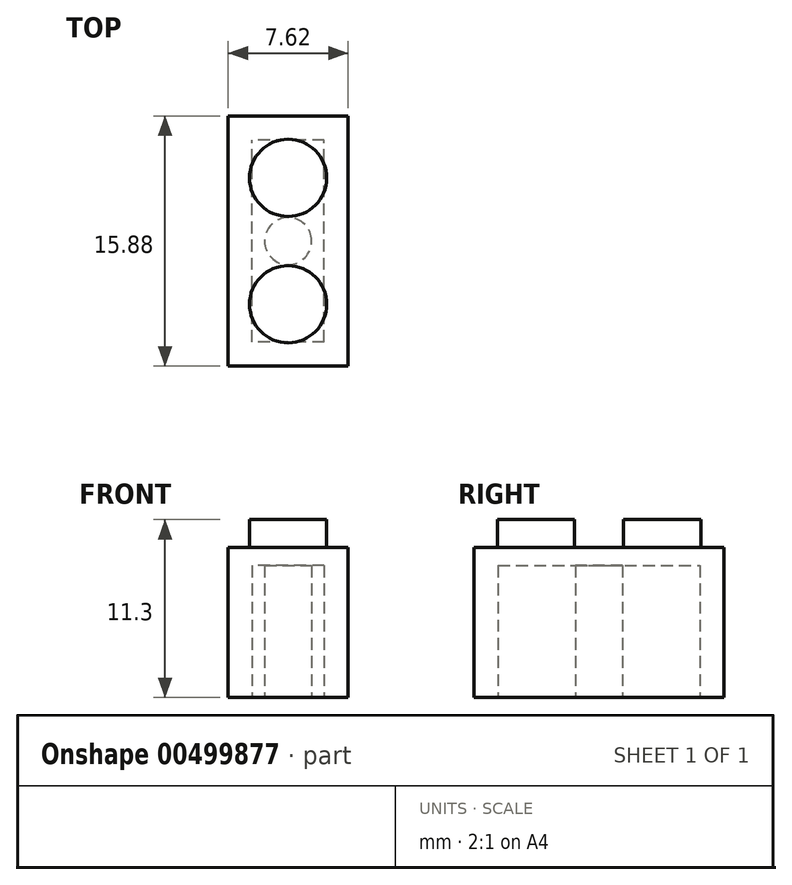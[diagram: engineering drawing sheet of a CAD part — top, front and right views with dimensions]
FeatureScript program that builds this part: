
annotation { "Feature Type Name" : "Feature", "Feature Type Description" : "" }
export const myFeature = defineFeature(function(context is Context, id is Id, definition is map)
    precondition{}
    {
        {
            var Q0;
            Q0=qCreatedBy(makeId("Top.planeOp"),FACE);
            var sketch = newSketch(context, id + "F0", { "sketchPlane" : qUnion([Q0])});
            skLineSegment(sketch, "E0.bottom", {"start": v(3.81, 7.94) * mm, "end": v(-3.8, 7.94) * mm});
            skLineSegment(sketch, "E0.top", {"start": v(3.8, -7.94) * mm, "end": v(-3.81, -7.94) * mm});
            skLineSegment(sketch, "E0.left", {"start": v(3.81, 7.94) * mm, "end": v(3.8, -7.94) * mm});
            skLineSegment(sketch, "E0.right", {"start": v(-3.8, 7.94) * mm, "end": v(-3.81, -7.94) * mm});
            skPoint(sketch, "E0.middle", {"position": v(0, 0) * mm});
            skSolve(sketch);
        }
        {
            var Q0;
            Q0=makeQuery(id+"F0.imprint","IMPRINT",FACE,{"disambiguationData":[TD([[makeQuery(id+"F0.imprint","IMPRINT",EDGE,{"derivedFrom":sQuery(id+"F0.wireOp",EDGE,"E0.bottom")}),1.0]])]});
            extrude(context, id + "F1", {"entities" : qUnion([Q0]), "endBound" : BoundingType.SYMMETRIC, "depth" : 9.52 * mm});
        }
        {
            var Q0;
            Q0=makeQuery(id+"F1.opExtrude","CAP_FACE",FACE,{"disambiguationData":[OSD([sQuery(id+"F0.wireOp",EDGE,"E0.bottom"),sQuery(id+"F0.wireOp",EDGE,"E0.top"),sQuery(id+"F0.wireOp",EDGE,"E0.left"),sQuery(id+"F0.wireOp",EDGE,"E0.right")])],"isStart":false});
            var sketch = newSketch(context, id + "F2", { "sketchPlane" : qUnion([Q0])});
            skCircle(sketch, "E1", {"center": v(0, 4.01) * mm, "radius": 2.45 * mm});
            skCircle(sketch, "E2", {"center": v(0, -4.01) * mm, "radius": 2.45 * mm});
            skSolve(sketch);
        }
        {
            var Q0;
            Q0=makeQuery(id+"F2.imprint","IMPRINT",FACE,{"disambiguationData":[TD([[makeQuery(id+"F2.imprint","IMPRINT",EDGE,{"derivedFrom":sQuery(id+"F2.wireOp",EDGE,"E1")}),1.0]])]});
            var Q1;
            Q1=makeQuery(id+"F2.imprint","IMPRINT",FACE,{"disambiguationData":[TD([[makeQuery(id+"F2.imprint","IMPRINT",EDGE,{"derivedFrom":sQuery(id+"F2.wireOp",EDGE,"E2")}),1.0]])]});
            extrude(context, id + "F3", {"entities" : qUnion([Q0, Q1]), "operationType" : NewBodyOperationType.ADD, "depth" : 1.78 * mm});
        }
        {
            var Q0;
            Q0=makeQuery(id+"F1.opExtrude","CAP_FACE",FACE,{"disambiguationData":[OSD([sQuery(id+"F0.wireOp",EDGE,"E0.bottom"),sQuery(id+"F0.wireOp",EDGE,"E0.top"),sQuery(id+"F0.wireOp",EDGE,"E0.left"),sQuery(id+"F0.wireOp",EDGE,"E0.right")])],"isStart":true});
            var sketch = newSketch(context, id + "F4", { "sketchPlane" : qUnion([Q0])});
            skLineSegment(sketch, "E3.bottom", {"start": v(2.29, 6.41) * mm, "end": v(-2.29, 6.41) * mm});
            skLineSegment(sketch, "E3.top", {"start": v(2.29, -6.41) * mm, "end": v(-2.29, -6.41) * mm});
            skLineSegment(sketch, "E3.left", {"start": v(2.29, 6.41) * mm, "end": v(2.29, -6.41) * mm});
            skLineSegment(sketch, "E3.right", {"start": v(-2.29, 6.41) * mm, "end": v(-2.29, -6.41) * mm});
            skPoint(sketch, "E3.middle", {"position": v(0, 0) * mm});
            skCircle(sketch, "E4", {"center": v(0, 0) * mm, "radius": 1.5 * mm});
            skSolve(sketch);
        }
        {
            var Q0;
            Q0=makeQuery(id+"F4.imprint","IMPRINT",FACE,{"disambiguationData":[TD([[makeQuery(id+"F4.imprint","IMPRINT",EDGE,{"derivedFrom":sQuery(id+"F4.wireOp",EDGE,"E3.bottom")}),1.0]])]});
            extrude(context, id + "F5", {"entities" : qUnion([Q0]), "operationType" : NewBodyOperationType.REMOVE, "oppositeDirection" : true, "depth" : 8.38 * mm});
        }
    });
